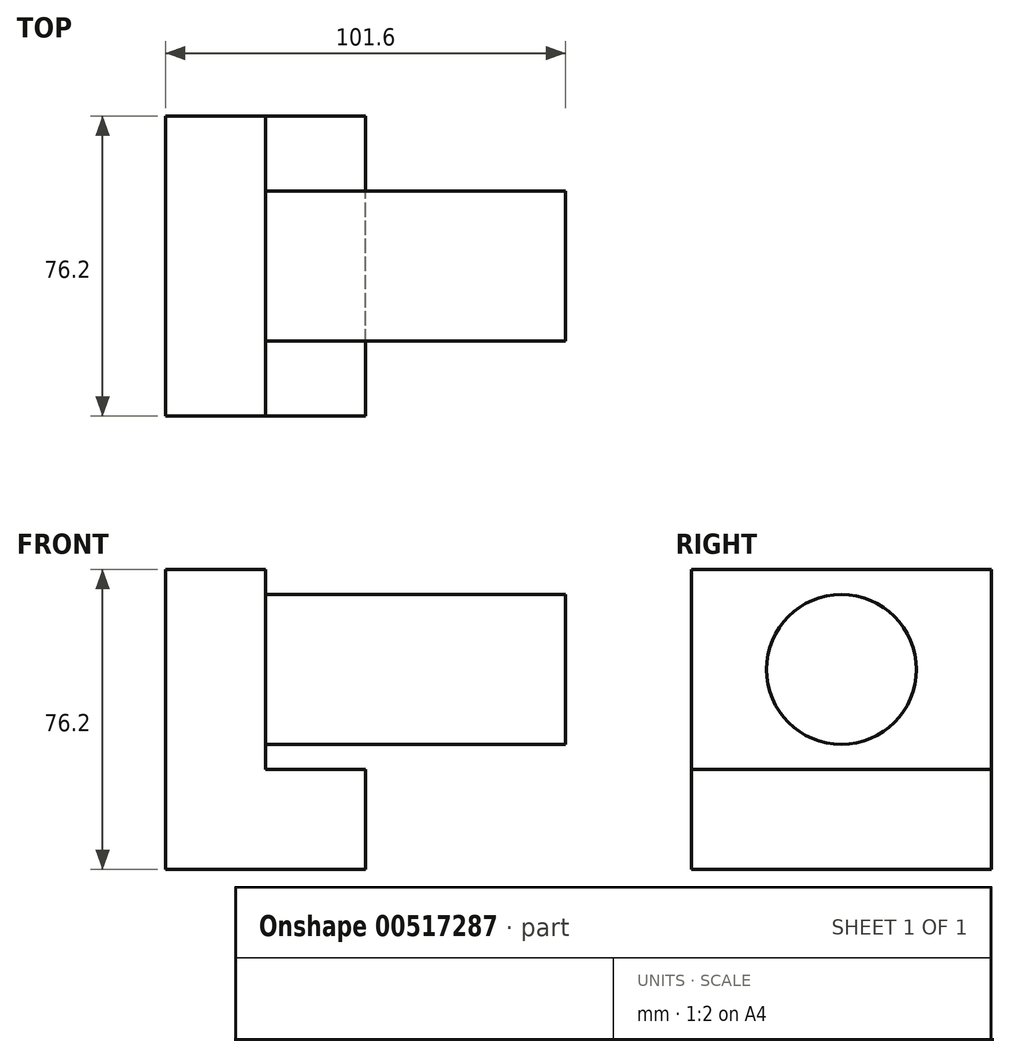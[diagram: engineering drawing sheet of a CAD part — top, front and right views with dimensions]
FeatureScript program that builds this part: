
annotation { "Feature Type Name" : "Feature", "Feature Type Description" : "" }
export const myFeature = defineFeature(function(context is Context, id is Id, definition is map)
    precondition{}
    {
        {
            var Q0;
            Q0=qCreatedBy(makeId("Front.planeOp"),FACE);
            var sketch = newSketch(context, id + "F0", { "sketchPlane" : qUnion([Q0])});
            skLineSegment(sketch, "E0", {"start": v(0, 0) * mm, "end": v(25.4, 0) * mm});
            skLineSegment(sketch, "E1", {"start": v(25.4, 0) * mm, "end": v(25.4, -25.4) * mm});
            skLineSegment(sketch, "E2", {"start": v(25.4, -25.4) * mm, "end": v(-25.4, -25.4) * mm});
            skLineSegment(sketch, "E3", {"start": v(-25.4, -25.4) * mm, "end": v(-25.4, 50.8) * mm});
            skLineSegment(sketch, "E4", {"start": v(-25.4, 50.8) * mm, "end": v(0, 50.8) * mm});
            skLineSegment(sketch, "E5", {"start": v(0, 50.8) * mm, "end": v(0, 0) * mm});
            skSolve(sketch);
        }
        {
            var Q0;
            Q0 = qSketchRegion(id + "F0", true);
            extrude(context, id + "F1", {"entities" : qUnion([Q0]), "depth" : 76.2 * mm, "offsetDistance" : 25.4 * mm});
        }
        {
            var Q0;
            Q0=makeQuery(id+"F1.opExtrude","SWEPT_FACE",FACE,{"disambiguationData":[OSD([sQuery(id+"F0.wireOp",EDGE,"E5")])]});
            var sketch = newSketch(context, id + "F2", { "sketchPlane" : qUnion([Q0])});
            skLineSegment(sketch, "E6", {"start": v(-76.2, 25.4) * mm, "end": v(0, 25.4) * mm, "construction": true});
            skLineSegment(sketch, "E7", {"start": v(-38.1, 50.8) * mm, "end": v(-38.1, 0) * mm, "construction": true});
            skCircle(sketch, "E8", {"center": v(-38.1, 25.4) * mm, "radius": 19.05 * mm});
            skSolve(sketch);
        }
        {
            var Q0;
            Q0 = qSketchRegion(id + "F2", true);
            extrude(context, id + "F3", {"entities" : qUnion([Q0]), "operationType" : NewBodyOperationType.ADD, "depth" : 76.2 * mm, "offsetDistance" : 25.4 * mm});
        }
    });
